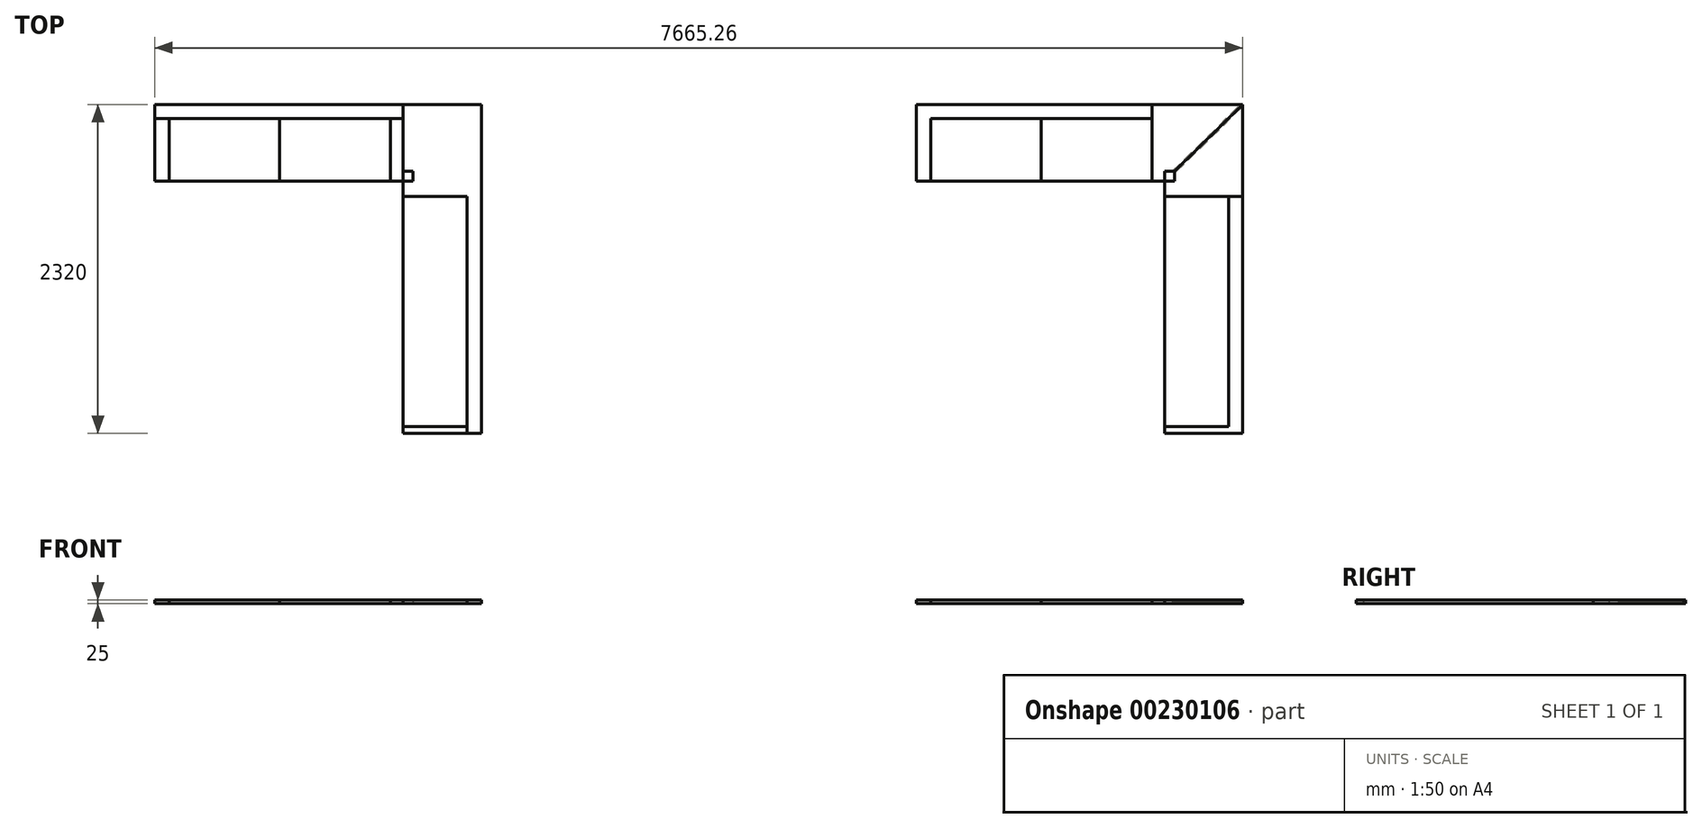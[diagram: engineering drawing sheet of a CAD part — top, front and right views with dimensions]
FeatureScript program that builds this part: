
annotation { "Feature Type Name" : "Feature", "Feature Type Description" : "" }
export const myFeature = defineFeature(function(context is Context, id is Id, definition is map)
    precondition{}
    {
        {
            var Q0;
            Q0=qCreatedBy(makeId("Top.planeOp"),FACE);
            var sketch = newSketch(context, id + "F0", { "sketchPlane" : qUnion([Q0])});
            skLineSegment(sketch, "E0.bottom", {"start": v(0, 0) * mm, "end": v(68, 0) * mm});
            skLineSegment(sketch, "E0.top", {"start": v(0, 68) * mm, "end": v(68, 68) * mm});
            skLineSegment(sketch, "E0.left", {"start": v(0, 0) * mm, "end": v(0, 68) * mm});
            skLineSegment(sketch, "E0.right", {"start": v(68, 0) * mm, "end": v(68, 68) * mm});
            skPoint(sketch, "E1.firstSnap0", {"position": v(0, 34) * mm});
            skLineSegment(sketch, "E1.bottom", {"start": v(0, 540) * mm, "end": v(550, 540) * mm});
            skLineSegment(sketch, "E1.top", {"start": v(0, -1780) * mm, "end": v(550, -1780) * mm});
            skLineSegment(sketch, "E1.left", {"start": v(0, 540) * mm, "end": v(0, -1780) * mm});
            skLineSegment(sketch, "E1.right", {"start": v(550, 540) * mm, "end": v(550, -1780) * mm});
            skLineSegment(sketch, "E2.bottom", {"start": v(0, 0) * mm, "end": v(-1750, 0) * mm});
            skLineSegment(sketch, "E2.top", {"start": v(0, 540) * mm, "end": v(-1750, 540) * mm});
            skLineSegment(sketch, "E2.left", {"start": v(0, 0) * mm, "end": v(0, 540) * mm});
            skLineSegment(sketch, "E2.right", {"start": v(-1750, 0) * mm, "end": v(-1750, 540) * mm});
            skLineSegment(sketch, "E3", {"start": v(-1650, 440) * mm, "end": v(-1650, 0) * mm});
            skLineSegment(sketch, "E4", {"start": v(-90, 440) * mm, "end": v(-90, 0) * mm});
            skLineSegment(sketch, "E5", {"start": v(-1650, 440) * mm, "end": v(-90, 440) * mm});
            skLineSegment(sketch, "E6", {"start": v(-90, 440) * mm, "end": v(0, 440) * mm});
            skLineSegment(sketch, "E7", {"start": v(-1650, 440) * mm, "end": v(-1750, 440) * mm});
            skLineSegment(sketch, "E8", {"start": v(-870, 440) * mm, "end": v(-870, 0) * mm});
            skLineSegment(sketch, "E9", {"start": v(0, -110) * mm, "end": v(550, -110) * mm});
            skLineSegment(sketch, "E10", {"start": v(0, -1730) * mm, "end": v(450, -1730) * mm});
            skLineSegment(sketch, "E11", {"start": v(450, -1730) * mm, "end": v(450, -110) * mm});
            skLineSegment(sketch, "E12", {"start": v(450, -1730) * mm, "end": v(450, -1780) * mm});
            skLineSegment(sketch, "E13.bottom", {"start": v(5365.26, 0) * mm, "end": v(5433.26, 0) * mm});
            skLineSegment(sketch, "E13.top", {"start": v(5365.26, 68) * mm, "end": v(5433.26, 68) * mm});
            skLineSegment(sketch, "E13.left", {"start": v(5365.26, 0) * mm, "end": v(5365.26, 68) * mm});
            skLineSegment(sketch, "E13.right", {"start": v(5433.26, 0) * mm, "end": v(5433.26, 68) * mm});
            skLineSegment(sketch, "E14.bottom", {"start": v(5275.26, 540) * mm, "end": v(5915.26, 540) * mm});
            skLineSegment(sketch, "E14.top", {"start": v(5365.26, -1780) * mm, "end": v(5915.26, -1780) * mm});
            skLineSegment(sketch, "E14.right", {"start": v(5915.26, 540) * mm, "end": v(5915.26, -1780) * mm});
            skLineSegment(sketch, "E15.bottom", {"start": v(5365.26, 0) * mm, "end": v(3615.26, 0) * mm});
            skLineSegment(sketch, "E15.top", {"start": v(5275.26, 540) * mm, "end": v(3615.26, 540) * mm});
            skLineSegment(sketch, "E15.right", {"start": v(3615.26, 0) * mm, "end": v(3615.26, 540) * mm});
            skLineSegment(sketch, "E16", {"start": v(3715.26, 440) * mm, "end": v(3715.26, 0) * mm});
            skLineSegment(sketch, "E17", {"start": v(5275.26, 440) * mm, "end": v(5275.26, 0) * mm});
            skLineSegment(sketch, "E18", {"start": v(3715.26, 440) * mm, "end": v(5275.26, 440) * mm});
            skLineSegment(sketch, "E19", {"start": v(4495.26, 440) * mm, "end": v(4495.26, 0) * mm});
            skLineSegment(sketch, "E20", {"start": v(5365.26, -110) * mm, "end": v(5915.26, -110) * mm});
            skLineSegment(sketch, "E21", {"start": v(5365.26, -1730) * mm, "end": v(5815.26, -1730) * mm});
            skLineSegment(sketch, "E22", {"start": v(5815.26, -1730) * mm, "end": v(5815.26, -110) * mm});
            skLineSegment(sketch, "E23.trimOffspring", {"start": v(5365.26, 68) * mm, "end": v(5365.26, -1780) * mm});
            skLineSegment(sketch, "E24", {"start": v(5275.26, 440) * mm, "end": v(5275.26, 540) * mm});
            skLineSegment(sketch, "E25", {"start": v(5433.26, 68) * mm, "end": v(5915.26, 540) * mm});
            skPoint(sketch, "E26.end.orphan", {"position": v(3615.26, 440) * mm});
            skSolve(sketch);
        }
        {
            var Q0;
            {var subQ3=sQuery(id+"F0.wireOp",EDGE,"E3");Q0=makeQuery(id+"F0.imprint","IMPRINT",FACE,{"disambiguationData":[TD([[makeQuery(id+"F0.imprint","IMPRINT",EDGE,{"derivedFrom":subQ3}),-1.0]])]});}
            var Q1;
            {var subQ0=sQuery(id+"F0.wireOp",EDGE,"E4");Q1=makeQuery(id+"F0.imprint","IMPRINT",FACE,{"disambiguationData":[TD([[makeQuery(id+"F0.imprint","IMPRINT",EDGE,{"derivedFrom":subQ0}),-1.0]])]});}
            var Q2;
            {var subQ4=sQuery(id+"F0.wireOp",EDGE,"E10");Q2=makeQuery(id+"F0.imprint","IMPRINT",FACE,{"disambiguationData":[TD([[makeQuery(id+"F0.imprint","IMPRINT",EDGE,{"derivedFrom":subQ4}),-1.0]])]});}
            var Q3;
            Q3=makeQuery(id+"F0.imprint","IMPRINT",FACE,{"disambiguationData":[TD([[makeQuery(id+"F0.imprint","IMPRINT",EDGE,{"derivedFrom":sQuery(id+"F0.wireOp",EDGE,"E15.top")}),1.0]])]});
            var Q4;
            {var subQ7=sQuery(id+"F0.wireOp",EDGE,"E13.bottom");Q4=makeQuery(id+"F0.imprint","IMPRINT",FACE,{"disambiguationData":[TD([[makeQuery(id+"F0.imprint","IMPRINT",EDGE,{"derivedFrom":subQ7}),-1.0]])]});}
            extrude(context, id + "F1", {"entities" : qUnion([Q0, Q1, Q2, Q3, Q4]), "depth" : 25 * mm});
        }
        {
            var Q0;
            {var subQ0=sQuery(id+"F0.wireOp",EDGE,"E11");Q0=makeQuery(id+"F0.imprint","IMPRINT",FACE,{"disambiguationData":[TD([[makeQuery(id+"F0.imprint","IMPRINT",EDGE,{"derivedFrom":subQ0}),-1.0]])]});}
            var Q1;
            {var subQ2=sQuery(id+"F0.wireOp",EDGE,"E0.bottom");Q1=makeQuery(id+"F0.imprint","IMPRINT",FACE,{"disambiguationData":[TD([[makeQuery(id+"F0.imprint","IMPRINT",EDGE,{"derivedFrom":subQ2}),-1.0]])]});}
            var Q2;
            {var subQ0=sQuery(id+"F0.wireOp",EDGE,"E3");Q2=makeQuery(id+"F0.imprint","IMPRINT",FACE,{"disambiguationData":[TD([[makeQuery(id+"F0.imprint","IMPRINT",EDGE,{"derivedFrom":subQ0}),1.0]])]});}
            var Q3;
            {var subQ0=sQuery(id+"F0.wireOp",EDGE,"E16");Q3=makeQuery(id+"F0.imprint","IMPRINT",FACE,{"disambiguationData":[TD([[makeQuery(id+"F0.imprint","IMPRINT",EDGE,{"derivedFrom":subQ0}),1.0]])]});}
            var Q4;
            {var subQ4=sQuery(id+"F0.wireOp",EDGE,"E13.top");Q4=makeQuery(id+"F0.imprint","IMPRINT",FACE,{"disambiguationData":[TD([[makeQuery(id+"F0.imprint","IMPRINT",EDGE,{"derivedFrom":subQ4}),1.0]])]});}
            var Q5;
            {var subQ4=sQuery(id+"F0.wireOp",EDGE,"E21");Q5=makeQuery(id+"F0.imprint","IMPRINT",FACE,{"disambiguationData":[TD([[makeQuery(id+"F0.imprint","IMPRINT",EDGE,{"derivedFrom":subQ4}),1.0]])]});}
            extrude(context, id + "F2", {"entities" : qUnion([Q0, Q1, Q2, Q3, Q4, Q5]), "depth" : 25 * mm});
        }
        {
            var Q0;
            {var subQ3=sQuery(id+"F0.wireOp",EDGE,"E10");Q0=makeQuery(id+"F0.imprint","IMPRINT",FACE,{"disambiguationData":[TD([[makeQuery(id+"F0.imprint","IMPRINT",EDGE,{"derivedFrom":subQ3}),1.0]])]});}
            var Q1;
            {var subQ4=sQuery(id+"F0.wireOp",EDGE,"E2.top");Q1=makeQuery(id+"F0.imprint","IMPRINT",FACE,{"disambiguationData":[TD([[makeQuery(id+"F0.imprint","IMPRINT",EDGE,{"derivedFrom":subQ4}),1.0]])]});}
            var Q2;
            {var subQ2=sQuery(id+"F0.wireOp",EDGE,"E14.top");Q2=makeQuery(id+"F0.imprint","IMPRINT",FACE,{"disambiguationData":[TD([[makeQuery(id+"F0.imprint","IMPRINT",EDGE,{"derivedFrom":subQ2}),1.0]])]});}
            var Q3;
            {var subQ0=sQuery(id+"F0.wireOp",EDGE,"E17");Q3=makeQuery(id+"F0.imprint","IMPRINT",FACE,{"disambiguationData":[TD([[makeQuery(id+"F0.imprint","IMPRINT",EDGE,{"derivedFrom":subQ0}),-1.0]])]});}
            extrude(context, id + "F3", {"entities" : qUnion([Q0, Q1, Q2, Q3]), "depth" : 25 * mm});
        }
        {
            var Q0;
            {var subQ0=sQuery(id+"F0.wireOp",EDGE,"E4");Q0=makeQuery(id+"F0.imprint","IMPRINT",FACE,{"disambiguationData":[TD([[makeQuery(id+"F0.imprint","IMPRINT",EDGE,{"derivedFrom":subQ0}),1.0]])]});}
            extrude(context, id + "F4", {"entities" : qUnion([Q0]), "depth" : 25 * mm});
        }
        {
            var Q0;
            Q0=makeQuery(id+"F1.opExtrude","CAP_VERTEX",VERTEX,{"disambiguationData":[OSD([sQuery(id+"F0.wireOp",EDGE,"E14.bottom"),sQuery(id+"F0.wireOp",EDGE,"E14.right"),sQuery(id+"F0.wireOp",EDGE,"E25")])],"isStart":false});
            var Q1;
            Q1=makeQuery(id+"F1.opExtrude","CAP_EDGE",EDGE,{"disambiguationData":[OSD([sQuery(id+"F0.wireOp",EDGE,"E25")])],"isStart":false});
            cPlane(context, id + "F5", {"entities" : qUnion([Q0, Q1]), "cplaneType" : CPlaneType.LINE_POINT, "offset" : 25 * mm, "width" : 150 * mm, "height" : 150 * mm});
        }
        {
            var Q0;
            Q0=qCreatedBy(id+"F5.planeOp",FACE);
            var sketch = newSketch(context, id + "F6", { "sketchPlane" : qUnion([Q0])});
            skLineSegment(sketch, "E27.0", {"start": v(-3752.83, 25) * mm, "end": v(-3752.83, 0) * mm});
            skLineSegment(sketch, "E28.bottom", {"start": v(-3762.83, 9) * mm, "end": v(-3742.83, 9) * mm});
            skLineSegment(sketch, "E28.top", {"start": v(-3762.83, 16) * mm, "end": v(-3742.83, 16) * mm});
            skLineSegment(sketch, "E28.left", {"start": v(-3762.83, 9) * mm, "end": v(-3762.83, 16) * mm});
            skLineSegment(sketch, "E28.right", {"start": v(-3742.83, 9) * mm, "end": v(-3742.83, 16) * mm});
            skPoint(sketch, "E28.middle", {"position": v(-3752.83, 12.5) * mm});
            skSolve(sketch);
        }
        {
            var Q0;
            {var subQ5=sQuery(id+"F6.wireOp",EDGE,"E28.right");Q0=makeQuery(id+"F6.imprint","IMPRINT",FACE,{"disambiguationData":[TD([[makeQuery(id+"F6.imprint","IMPRINT",EDGE,{"derivedFrom":subQ5}),1.0]])]});}
            var Q1;
            {var subQ5=sQuery(id+"F6.wireOp",EDGE,"E28.left");Q1=makeQuery(id+"F6.imprint","IMPRINT",FACE,{"disambiguationData":[TD([[makeQuery(id+"F6.imprint","IMPRINT",EDGE,{"derivedFrom":subQ5}),-1.0]])]});}
            var Q2;
            Q2=makeQuery(id+"F2.opExtrude","SWEPT_FACE",FACE,{"disambiguationData":[OSD([sQuery(id+"F0.wireOp",EDGE,"E13.top")])]});
            var Q3;
            Q3=makeQuery(id+"F1.opExtrude","CAP_VERTEX",VERTEX,{"disambiguationData":[OSD([sQuery(id+"F0.wireOp",EDGE,"E13.bottom"),sQuery(id+"F0.wireOp",EDGE,"E15.bottom"),sQuery(id+"F0.wireOp",EDGE,"E23.trimOffspring")])],"isStart":false});
            extrude(context, id + "F7", {"entities" : qUnion([Q0, Q1]), "endBound" : BoundingType.UP_TO_SURFACE, "oppositeDirection" : true, "endBoundEntityFace" : qUnion([Q2]), "endBoundEntityVertex" : qUnion([Q3]), "depth" : 25 * mm});
        }
        {
            var Q0;
            Q0=makeQuery(id+"F7.opExtrude","SWEPT_BODY",BODY,{"disambiguationData":[OSD([sQuery(id+"F6.wireOp",EDGE,"E28.bottom"),sQuery(id+"F6.wireOp",EDGE,"E28.top"),sQuery(id+"F6.wireOp",EDGE,"E28.left"),sQuery(id+"F6.wireOp",EDGE,"E28.right")])]});
            var Q1;
            Q1=makeQuery(id+"F2.opExtrude","SWEPT_BODY",BODY,{"disambiguationData":[OSD([sQuery(id+"F0.wireOp",EDGE,"E13.top"),sQuery(id+"F0.wireOp",EDGE,"E14.bottom"),sQuery(id+"F0.wireOp",EDGE,"E15.bottom"),sQuery(id+"F0.wireOp",EDGE,"E17"),sQuery(id+"F0.wireOp",EDGE,"E23.trimOffspring"),sQuery(id+"F0.wireOp",EDGE,"E24"),sQuery(id+"F0.wireOp",EDGE,"E25")])]});
            var Q2;
            Q2=makeQuery(id+"F1.opExtrude","SWEPT_BODY",BODY,{"disambiguationData":[OSD([sQuery(id+"F0.wireOp",EDGE,"E13.bottom"),sQuery(id+"F0.wireOp",EDGE,"E13.right"),sQuery(id+"F0.wireOp",EDGE,"E14.right"),sQuery(id+"F0.wireOp",EDGE,"E20"),sQuery(id+"F0.wireOp",EDGE,"E23.trimOffspring"),sQuery(id+"F0.wireOp",EDGE,"E25")])]});
            booleanBodies(context, id + "F8", {"operationType" : BooleanOperationType.SUBTRACTION, "tools" : qUnion([Q0]), "targets" : qUnion([Q1, Q2])});
        }
    });
